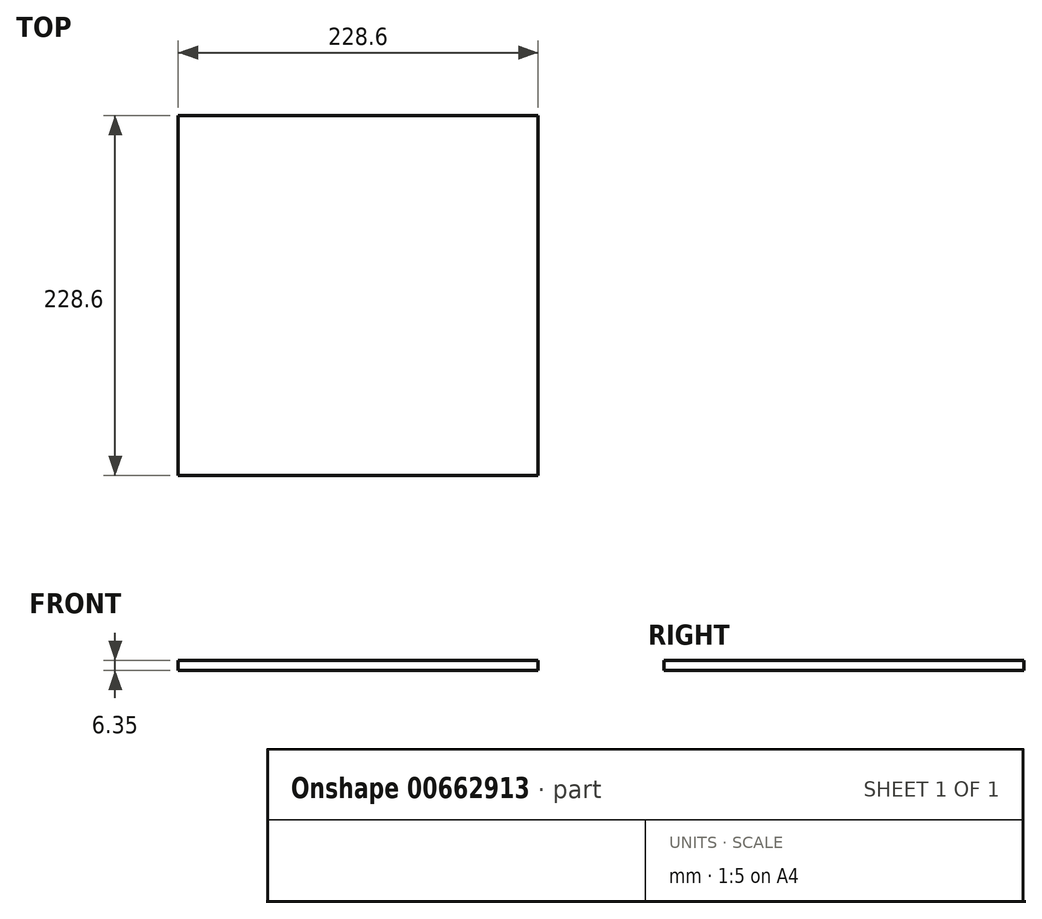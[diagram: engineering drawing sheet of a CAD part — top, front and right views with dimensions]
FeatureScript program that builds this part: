
annotation { "Feature Type Name" : "Feature", "Feature Type Description" : "" }
export const myFeature = defineFeature(function(context is Context, id is Id, definition is map)
    precondition{}
    {
        {
            var Q0;
            Q0=qCreatedBy(makeId("Top.planeOp"),FACE);
            var sketch = newSketch(context, id + "F0", { "sketchPlane" : qUnion([Q0])});
            skLineSegment(sketch, "E0.bottom", {"start": v(-218.18, 195.36) * mm, "end": v(10.42, 195.36) * mm});
            skLineSegment(sketch, "E0.top", {"start": v(-218.18, -33.24) * mm, "end": v(10.42, -33.24) * mm});
            skLineSegment(sketch, "E0.left", {"start": v(-218.18, 195.36) * mm, "end": v(-218.18, -33.24) * mm});
            skLineSegment(sketch, "E0.right", {"start": v(10.42, 195.36) * mm, "end": v(10.42, -33.24) * mm});
            skSolve(sketch);
        }
        {
            var Q0;
            Q0 = qSketchRegion(id + "F0", true);
            extrude(context, id + "F1", {"entities" : qUnion([Q0]), "depth" : 6.35 * mm, "offsetDistance" : 25.4 * mm});
        }
    });
